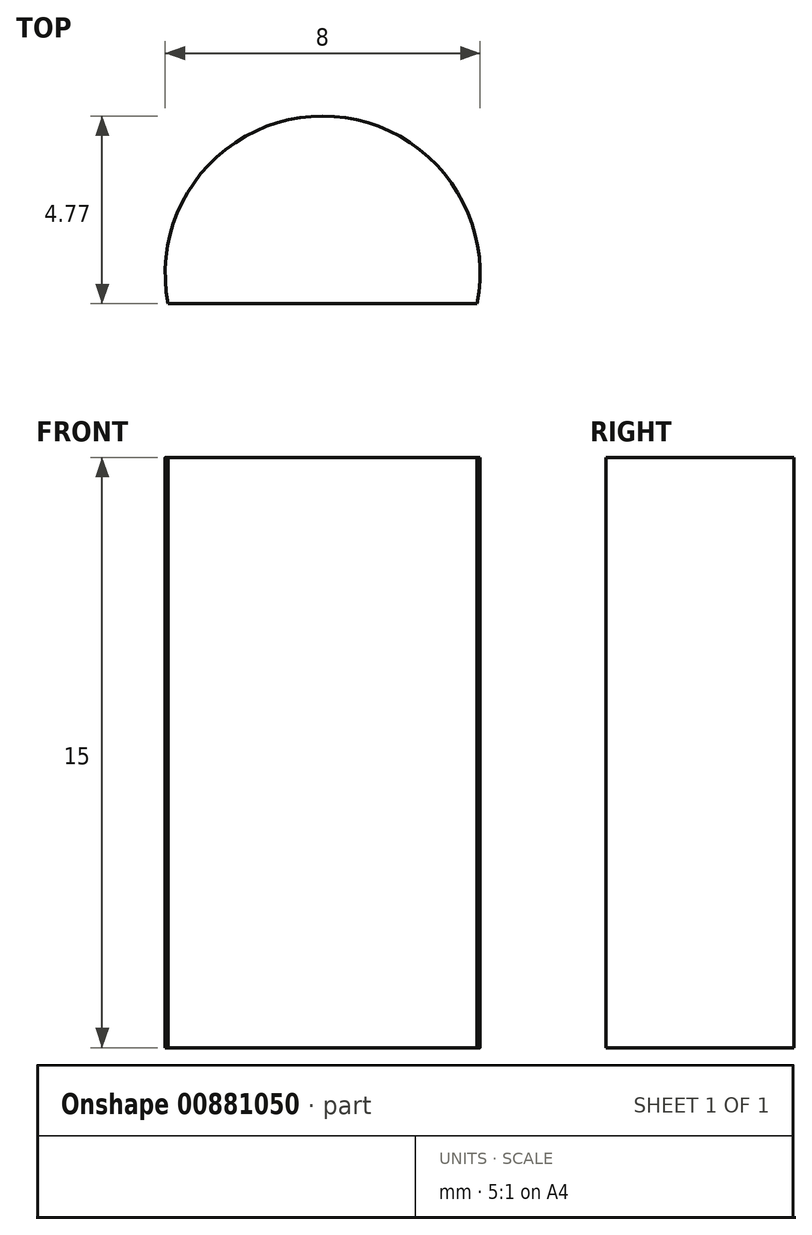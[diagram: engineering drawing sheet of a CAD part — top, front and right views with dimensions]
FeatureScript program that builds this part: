
annotation { "Feature Type Name" : "Feature", "Feature Type Description" : "" }
export const myFeature = defineFeature(function(context is Context, id is Id, definition is map)
    precondition{}
    {
        {
            var Q0;
            Q0=qCreatedBy(makeId("Top.planeOp"),FACE);
            var sketch = newSketch(context, id + "F0", { "sketchPlane" : qUnion([Q0])});
            skArc(sketch, "E0", {"start": v(3.93, -0.77) * mm, "mid": v(0, 4) * mm, "end": v(-3.93, -0.77) * mm});
            skLineSegment(sketch, "E1", {"start": v(-3.93, -0.77) * mm, "end": v(3.93, -0.77) * mm});
            skSolve(sketch);
        }
        {
            var Q0;
            Q0 = qSketchRegion(id + "F0", true);
            extrude(context, id + "F1", {"entities" : qUnion([Q0]), "depth" : 15 * mm, "offsetDistance" : 25 * mm});
        }
    });
